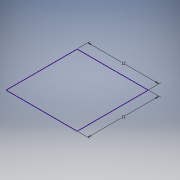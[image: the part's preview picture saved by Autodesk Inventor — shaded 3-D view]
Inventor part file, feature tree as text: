
AUTODESK INVENTOR PART (.ipt)
format: ipt  version: 2017 (Build 210142000, 142)  size: 84,992 bytes
history: native  units: mm
features: sketch x1
ambient origin geometry x8: Origin, YZ Plane, XZ Plane, XY Plane, X Axis, Y Axis, Z Axis, Center Point
feature tree (1):
  sketch  "Sketch1"  dims[d0=12.0mm d1=12.0mm]
